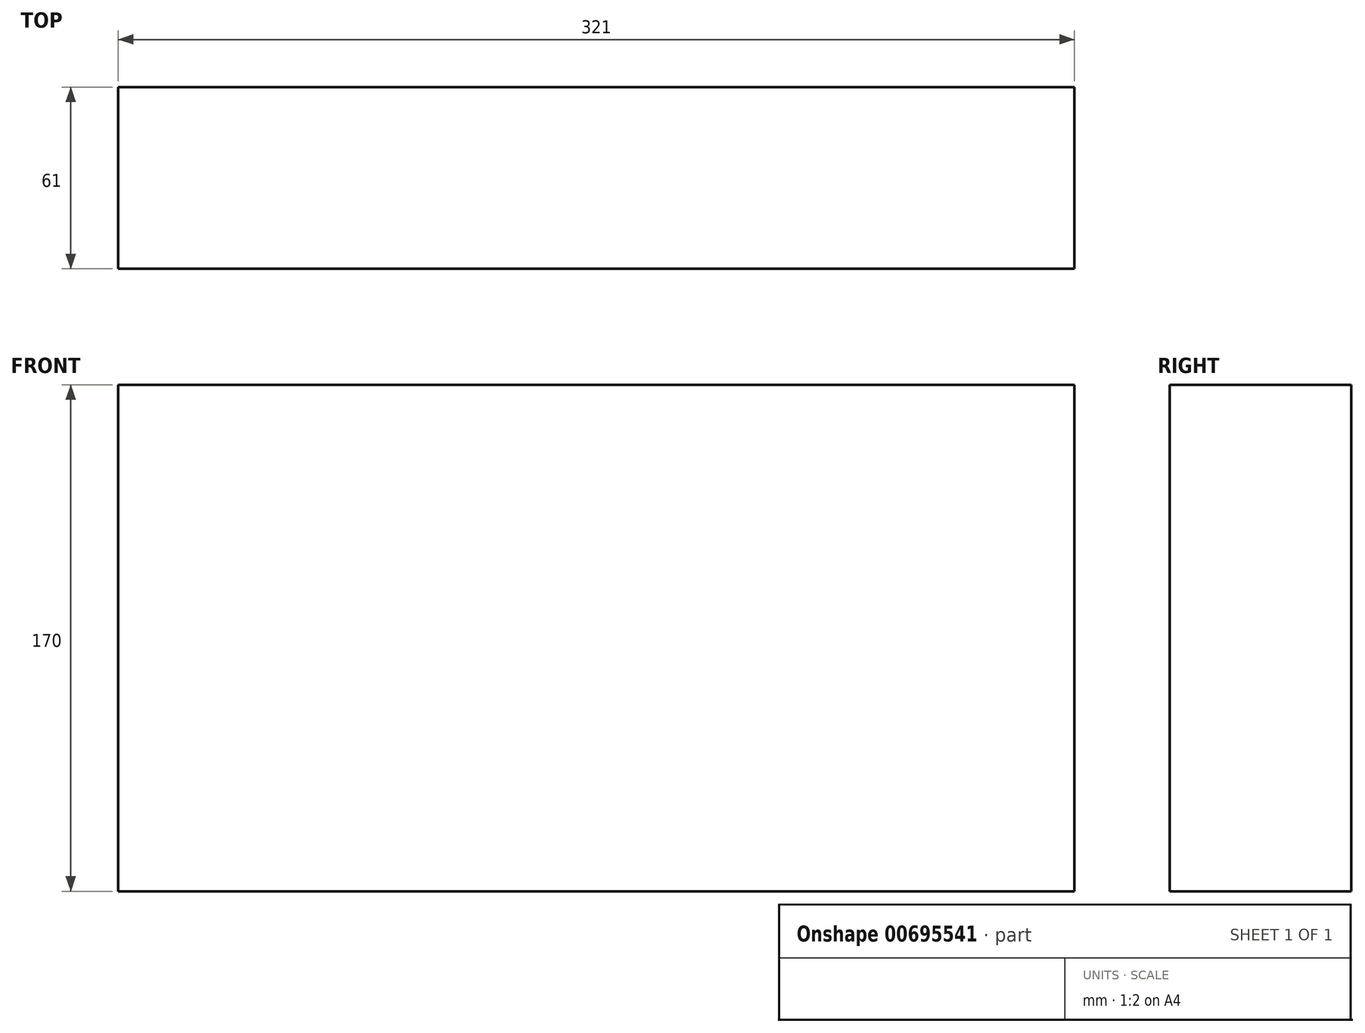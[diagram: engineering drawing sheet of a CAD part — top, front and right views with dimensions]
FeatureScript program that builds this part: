
annotation { "Feature Type Name" : "Feature", "Feature Type Description" : "" }
export const myFeature = defineFeature(function(context is Context, id is Id, definition is map)
    precondition{}
    {
        {
            var Q0;
            Q0=qCreatedBy(makeId("Top.planeOp"),FACE);
            var sketch = newSketch(context, id + "F0", { "sketchPlane" : qUnion([Q0])});
            skLineSegment(sketch, "E0.bottom", {"start": v(-159.86, 31.87) * mm, "end": v(161.14, 31.87) * mm});
            skLineSegment(sketch, "E0.top", {"start": v(-159.86, -29.13) * mm, "end": v(161.14, -29.13) * mm});
            skLineSegment(sketch, "E0.left", {"start": v(-159.86, 31.87) * mm, "end": v(-159.86, -29.13) * mm});
            skLineSegment(sketch, "E0.right", {"start": v(161.14, 31.87) * mm, "end": v(161.14, -29.13) * mm});
            skSolve(sketch);
        }
        {
            var Q0;
            Q0 = qSketchRegion(id + "F0", true);
            extrude(context, id + "F1", {"entities" : qUnion([Q0]), "depth" : 170 * mm, "offsetDistance" : 25 * mm});
        }
    });
